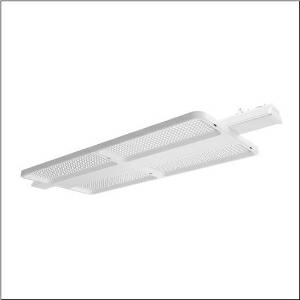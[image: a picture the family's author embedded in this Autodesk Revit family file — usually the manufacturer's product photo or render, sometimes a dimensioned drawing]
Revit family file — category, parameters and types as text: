
# Revit family: highbay_11_fur_licross_r__tragschiene_maxi_51hn11db3mla_2453
name_source: partatom
category: Lighting Fixtures
units: mm (PartAtom-declared; Revit-internal decimal feet)

## family parameters
Cut with Voids When Loaded = No
Host = Face
Light Source = No
Part Type = Normal
Room Calculation Point = No
Round Connector Dimension = Use Diameter
Shared = No

## types (1)
- --- (1 x LED, 28480 lm, 146.3 W, 3000K)
    Apparent Load = 146 VA
    CIE Flux Codes = 85 97 100 100 100
    Color Rendering = 80
    Color Temperature = 3000K
    Default Elevation = 1800 mm
    Description = high bay luminaire Highbay 11 for Licross® trunking rail maxi; direct symmetric narrow distribution, light control with lens of PMMA; UGR ≤ 22 (X = 4H | Y = 8H | S = 0.25H | reflection values 70/50/20); luminous flux: 28.480lm; light colour: 830, colour temperature: 3000K, MacAdam ≤ 2 SDCM (initial), colour rendering: CRI > 80; luminous efficacy: 194,7lm/W; rated service life: 100.000h (L95/B50) at AT= 25°C; control: DALI 2; luminaire connection: plug, 5-pole, with phase selectionmains connection: 230..240V, AC 50/60Hz; connected load: 146,3W; protection rating (complete): IP64; insulation class (complete): insulation class I (protective earthing); protection symbol: D; impact resistance: IK07; certification: CE, ENEC, VDE, UKCA; internal wiring halogen-free; luminaire LABS conformity tested according to VDMA 24364:2018-05; corresponds to IFS (International Featured Standards) requirements for safety and quality in the food industry; housing frame of high-performance plastic PA6, matt traffic white (RAL 9016); cover of PMMA; fixing on rail side of steel, galvanised, white; blank cover of PC/ABS, traffic white (RAL 9016); dimension (LxWxH): 1.250 x 442 x 71mm; permissible operating ambient temperature: -40..+55°C (reducing of maximum allowable ambient temperature of 5°C with ceiling mounting); packaging unit: 1 piece
    Height = 72 mm  [stored 0.23622 ft]
    Lamp = 1 x LED
    Lamp Light Flux = 28480 lm
    Lamp Power = 146.3 W
    Lamp count = 1
    Length = 946 mm
    Luminous efficacy = 195 lm/W
    Manufacturer = Siteco
    ModVariant = No
    Model = 51HN11DB3MLA
    Mounting Place = Ceiling
    Mounting Type = Pendant
    Number of Poles = 1
    OnlyDefault = Yes
    Power Factor = 1
    Product Name = Highbay 11 für Licross® Tragschiene maxi
    Product group = high bay luminaire
    ProductGroupID = 901
    Protection Class = Protection class I
    Protection Degree = IP 64
    RLX_Detail_Level = 1
    RLX_Emergency_Light_Flux = 0 lm
    RLX_Emergency_Type = 0
    RLX_Emergency_Type_DB = No
    RlxData = <blob elided: 24337 chars, md5=d6e1c2e3>
    Socket = socket
    Standby Power = 0 W
    System Light Flux = 28480 lm
    System Power = 146 W
    Type Comments = factory setting: luminous flux: 100 % | dim-lin: 254 | 678 mA
    Type Image = l_1361711.jpg
    URL = http://relux.com
    VarID = @adj_005345
    Voltage = 0 V
    Weight = 0.00 kg
    Width = 442 mm

note: [stored X ft] marks values corroborated as IEEE doubles in the binary element streams (Revit-internal decimal feet)

## geometry (parser evidence)
native form markers: Blend x4, Sweep x10
no freeform markers — native parametric forms only
